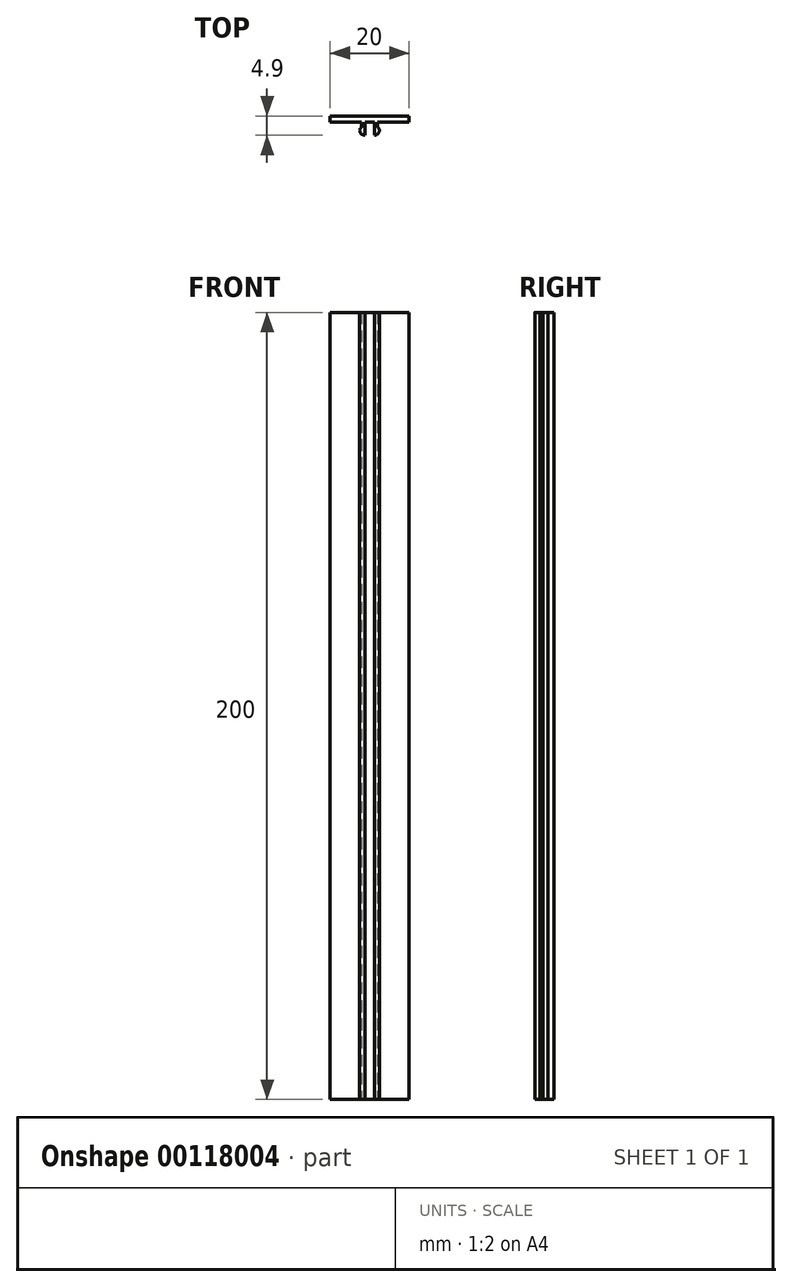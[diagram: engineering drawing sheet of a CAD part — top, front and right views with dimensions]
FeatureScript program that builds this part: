
annotation { "Feature Type Name" : "Feature", "Feature Type Description" : "" }
export const myFeature = defineFeature(function(context is Context, id is Id, definition is map)
    precondition{}
    {
        {
            var Q0;
            Q0=qCreatedBy(makeId("Top.planeOp"),FACE);
            var sketch = newSketch(context, id + "F0", { "sketchPlane" : qUnion([Q0])});
            skLineSegment(sketch, "E0", {"start": v(-10, 3.3) * mm, "end": v(-10, 4.9) * mm});
            skLineSegment(sketch, "E1", {"start": v(-10, 4.9) * mm, "end": v(10, 4.9) * mm});
            skLineSegment(sketch, "E2", {"start": v(10, 4.9) * mm, "end": v(10, 3.3) * mm});
            skLineSegment(sketch, "E3", {"start": v(10, 3.3) * mm, "end": v(2, 3.3) * mm});
            skLineSegment(sketch, "E4", {"start": v(2, 3.3) * mm, "end": v(2, 2) * mm});
            skLineSegment(sketch, "E5", {"start": v(2, 2) * mm, "end": v(2.5, 2) * mm});
            skLineSegment(sketch, "E6", {"start": v(2.5, 2) * mm, "end": v(2.5, 0.8) * mm});
            skLineSegment(sketch, "E7", {"start": v(1.2, 0.8) * mm, "end": v(1.2, 3.3) * mm});
            skLineSegment(sketch, "E8", {"start": v(1.2, 3.3) * mm, "end": v(-1.2, 3.3) * mm});
            skLineSegment(sketch, "E9", {"start": v(-1.2, 3.3) * mm, "end": v(-1.2, 0.8) * mm});
            skLineSegment(sketch, "E10", {"start": v(-1.2, 0.8) * mm, "end": v(-1.2, 0.8) * mm});
            skLineSegment(sketch, "E11", {"start": v(-2.5, 0.8) * mm, "end": v(-2.5, 2) * mm});
            skLineSegment(sketch, "E12", {"start": v(-2.5, 2) * mm, "end": v(-2, 2) * mm});
            skLineSegment(sketch, "E13", {"start": v(-2, 3.3) * mm, "end": v(-10, 3.3) * mm});
            skLineSegment(sketch, "E14", {"start": v(0, 0) * mm, "end": v(0, 8.4) * mm, "construction": true});
            skPoint(sketch, "E14.startSnap0", {"position": v(0, 4.9) * mm});
            skLineSegment(sketch, "E15", {"start": v(1.2, 0.8) * mm, "end": v(1.2, 0.8) * mm});
            skLineSegment(sketch, "E16", {"start": v(-2.5, 0.8) * mm, "end": v(-2.5, 0) * mm});
            skLineSegment(sketch, "E17", {"start": v(-2.5, 0) * mm, "end": v(-1.2, 0) * mm});
            skLineSegment(sketch, "E18", {"start": v(-1.2, 0) * mm, "end": v(-1.2, 0.8) * mm});
            skLineSegment(sketch, "E19", {"start": v(2.5, 0.8) * mm, "end": v(2.5, 0) * mm});
            skLineSegment(sketch, "E20", {"start": v(2.5, 0) * mm, "end": v(1.2, 0) * mm});
            skLineSegment(sketch, "E21", {"start": v(1.2, 0) * mm, "end": v(1.2, 0.8) * mm});
            skLineSegment(sketch, "E22", {"start": v(-2, 2) * mm, "end": v(-2, 3.3) * mm});
            skSolve(sketch);
        }
        {
            var Q0;
            Q0 = qSketchRegion(id + "F0", true);
            extrude(context, id + "F1", {"entities" : qUnion([Q0]), "depth" : 200 * mm});
        }
        {
            var Q0;
            Q0=makeQuery(id+"F1.opExtrude","SWEPT_EDGE",EDGE,{"disambiguationData":[OSD([sQuery(id+"F0.wireOp",EDGE,"E5"),sQuery(id+"F0.wireOp",EDGE,"E6")])]});
            var Q1;
            Q1=makeQuery(id+"F1.opExtrude","SWEPT_EDGE",EDGE,{"disambiguationData":[OSD([sQuery(id+"F0.wireOp",EDGE,"E11"),sQuery(id+"F0.wireOp",EDGE,"E12")])]});
            fillet(context, id + "F2", {"entities" : qUnion([Q0, Q1]), "radius" : 0.8 * mm, "tangentPropagation" : true, "allowEdgeOverflow" : false});
        }
        {
            var Q0;
            Q0=makeQuery(id+"F1.opExtrude","SWEPT_EDGE",EDGE,{"disambiguationData":[OSD([sQuery(id+"F0.wireOp",EDGE,"E16"),sQuery(id+"F0.wireOp",EDGE,"E17")])]});
            var Q1;
            Q1=makeQuery(id+"F1.opExtrude","SWEPT_EDGE",EDGE,{"disambiguationData":[OSD([sQuery(id+"F0.wireOp",EDGE,"E19"),sQuery(id+"F0.wireOp",EDGE,"E20")])]});
            fillet(context, id + "F3", {"entities" : qUnion([Q0, Q1]), "radius" : 1.3 * mm, "tangentPropagation" : true, "allowEdgeOverflow" : false});
        }
    });
